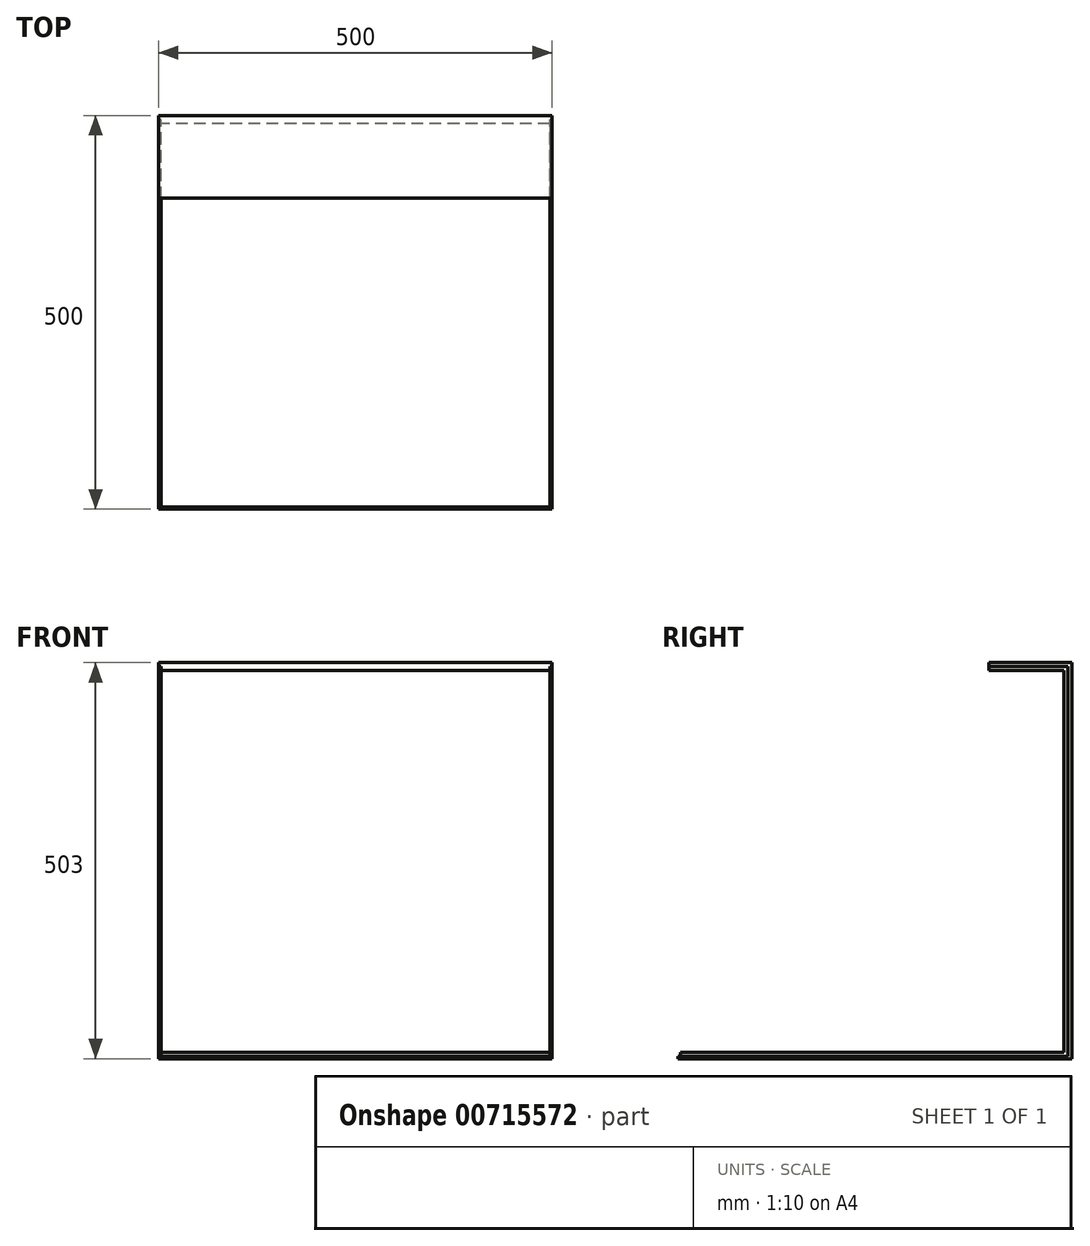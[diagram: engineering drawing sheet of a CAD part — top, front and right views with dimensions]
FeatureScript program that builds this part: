
annotation { "Feature Type Name" : "Feature", "Feature Type Description" : "" }
export const myFeature = defineFeature(function(context is Context, id is Id, definition is map)
    precondition{}
    {
        {
            var Q0;
            Q0=qCreatedBy(makeId("Top.planeOp"),FACE);
            var sketch = newSketch(context, id + "F0", { "sketchPlane" : qUnion([Q0])});
            skLineSegment(sketch, "E0.bottom", {"start": v(-250, 250) * mm, "end": v(250, 250) * mm});
            skLineSegment(sketch, "E0.top", {"start": v(-250, -250) * mm, "end": v(250, -250) * mm});
            skLineSegment(sketch, "E0.left", {"start": v(-250, 250) * mm, "end": v(-250, -250) * mm});
            skLineSegment(sketch, "E0.right", {"start": v(250, 250) * mm, "end": v(250, -250) * mm});
            skPoint(sketch, "E0.middle", {"position": v(0, 0) * mm});
            skSolve(sketch);
        }
        {
            var Q0;
            Q0=makeQuery(id+"F0.imprint","IMPRINT",FACE,{"disambiguationData":[TD([[makeQuery(id+"F0.imprint","IMPRINT",EDGE,{"derivedFrom":sQuery(id+"F0.wireOp",EDGE,"E0.bottom")}),-1.0]])]});
            extrude(context, id + "F1", {"entities" : qUnion([Q0]), "depth" : 3 * mm, "offsetDistance" : 25 * mm});
        }
        {
            var Q0;
            Q0=makeQuery(id+"F1.opExtrude","CAP_FACE",FACE,{"disambiguationData":[OSD([sQuery(id+"F0.wireOp",EDGE,"E0.bottom"),sQuery(id+"F0.wireOp",EDGE,"E0.top"),sQuery(id+"F0.wireOp",EDGE,"E0.left"),sQuery(id+"F0.wireOp",EDGE,"E0.right")])],"isStart":false});
            var sketch = newSketch(context, id + "F2", { "sketchPlane" : qUnion([Q0])});
            skLineSegment(sketch, "E1.bottom", {"start": v(-247, -247) * mm, "end": v(247, -247) * mm});
            skLineSegment(sketch, "E1.top", {"start": v(-247, 245) * mm, "end": v(247, 245) * mm});
            skLineSegment(sketch, "E1.left", {"start": v(-247, -247) * mm, "end": v(-247, 245) * mm});
            skLineSegment(sketch, "E1.right", {"start": v(247, -247) * mm, "end": v(247, 245) * mm});
            skSolve(sketch);
        }
        {
            var Q0;
            Q0 = qSketchRegion(id + "F2", true);
            extrude(context, id + "F3", {"entities" : qUnion([Q0]), "operationType" : NewBodyOperationType.ADD, "depth" : 5 * mm, "offsetDistance" : 25 * mm});
        }
        {
            var Q0;
            Q0=makeQuery(id+"F1.opExtrude","CAP_FACE",FACE,{"disambiguationData":[OSD([sQuery(id+"F0.wireOp",EDGE,"E0.bottom"),sQuery(id+"F0.wireOp",EDGE,"E0.top"),sQuery(id+"F0.wireOp",EDGE,"E0.left"),sQuery(id+"F0.wireOp",EDGE,"E0.right")])],"isStart":false});
            var sketch = newSketch(context, id + "F4", { "sketchPlane" : qUnion([Q0])});
            skLineSegment(sketch, "E2.bottom", {"start": v(250, 250) * mm, "end": v(-250, 250) * mm});
            skLineSegment(sketch, "E2.top", {"start": v(250, 245) * mm, "end": v(-250, 245) * mm});
            skLineSegment(sketch, "E2.left", {"start": v(250, 250) * mm, "end": v(250, 245) * mm});
            skLineSegment(sketch, "E2.right", {"start": v(-250, 250) * mm, "end": v(-250, 245) * mm});
            skSolve(sketch);
        }
        {
            var Q0;
            Q0 = qSketchRegion(id + "F4", true);
            extrude(context, id + "F5", {"entities" : qUnion([Q0]), "operationType" : NewBodyOperationType.ADD, "depth" : 500 * mm, "offsetDistance" : 25 * mm});
        }
        {
            var Q0;
            Q0=makeQuery(id+"F5.opExtrude","SWEPT_FACE",FACE,{"disambiguationData":[OSD([sQuery(id+"F4.wireOp",EDGE,"E2.top")])]});
            var sketch = newSketch(context, id + "F6", { "sketchPlane" : qUnion([Q0])});
            skLineSegment(sketch, "E3.bottom", {"start": v(247, 8) * mm, "end": v(-247, 8) * mm});
            skLineSegment(sketch, "E3.top", {"start": v(247, 498) * mm, "end": v(-247, 498) * mm});
            skLineSegment(sketch, "E3.left", {"start": v(247, 8) * mm, "end": v(247, 498) * mm});
            skLineSegment(sketch, "E3.right", {"start": v(-247, 8) * mm, "end": v(-247, 498) * mm});
            skSolve(sketch);
        }
        {
            var Q0;
            Q0=makeQuery(id+"F6.imprint","IMPRINT",FACE,{"disambiguationData":[TD([[makeQuery(id+"F6.imprint","IMPRINT",EDGE,{"derivedFrom":sQuery(id+"F6.wireOp",EDGE,"E3.bottom")}),1.0]])]});
            extrude(context, id + "F7", {"entities" : qUnion([Q0]), "operationType" : NewBodyOperationType.ADD, "depth" : 5 * mm, "offsetDistance" : 25 * mm});
        }
        {
            var Q0;
            Q0=makeQuery(id+"F5.opExtrude","SWEPT_FACE",FACE,{"disambiguationData":[OSD([sQuery(id+"F4.wireOp",EDGE,"E2.top")])]});
            var sketch = newSketch(context, id + "F8", { "sketchPlane" : qUnion([Q0])});
            skLineSegment(sketch, "E4.bottom", {"start": v(250, 503) * mm, "end": v(-250, 503) * mm});
            skLineSegment(sketch, "E4.top", {"start": v(250, 498) * mm, "end": v(-250, 498) * mm});
            skLineSegment(sketch, "E4.left", {"start": v(250, 503) * mm, "end": v(250, 498) * mm});
            skLineSegment(sketch, "E4.right", {"start": v(-250, 503) * mm, "end": v(-250, 498) * mm});
            skSolve(sketch);
        }
        {
            var Q0;
            Q0 = qSketchRegion(id + "F8", true);
            extrude(context, id + "F9", {"entities" : qUnion([Q0]), "operationType" : NewBodyOperationType.ADD, "depth" : 100 * mm, "offsetDistance" : 25 * mm});
        }
        {
            var Q0;
            Q0=makeQuery(id+"F9.opExtrude","SWEPT_FACE",FACE,{"disambiguationData":[OSD([sQuery(id+"F8.wireOp",EDGE,"E4.top")])]});
            var sketch = newSketch(context, id + "F10", { "sketchPlane" : qUnion([Q0])});
            skLineSegment(sketch, "E5.bottom", {"start": v(-247, -240) * mm, "end": v(247, -240) * mm});
            skLineSegment(sketch, "E5.top", {"start": v(-247, -145) * mm, "end": v(247, -145) * mm});
            skLineSegment(sketch, "E5.left", {"start": v(-247, -240) * mm, "end": v(-247, -145) * mm});
            skLineSegment(sketch, "E5.right", {"start": v(247, -240) * mm, "end": v(247, -145) * mm});
            skSolve(sketch);
        }
        {
            var Q0;
            Q0=makeQuery(id+"F10.imprint","IMPRINT",FACE,{"disambiguationData":[TD([[makeQuery(id+"F10.imprint","IMPRINT",EDGE,{"derivedFrom":sQuery(id+"F10.wireOp",EDGE,"E5.bottom")}),-1.0]])]});
            var sketch = newSketch(context, id + "F11", { "sketchPlane" : qUnion([Q0])});
            skSolve(sketch);
        }
        {
            var Q0;
            Q0 = qSketchRegion(id + "F11", true);
            var Q1;
            Q1=makeQuery(id+"F10.imprint","IMPRINT",FACE,{"disambiguationData":[TD([[makeQuery(id+"F10.imprint","IMPRINT",EDGE,{"derivedFrom":sQuery(id+"F10.wireOp",EDGE,"E5.bottom")}),-1.0]])]});
            extrude(context, id + "F12", {"entities" : qUnion([Q0, Q1]), "operationType" : NewBodyOperationType.ADD, "depth" : 5 * mm, "offsetDistance" : 25 * mm});
        }
    });
